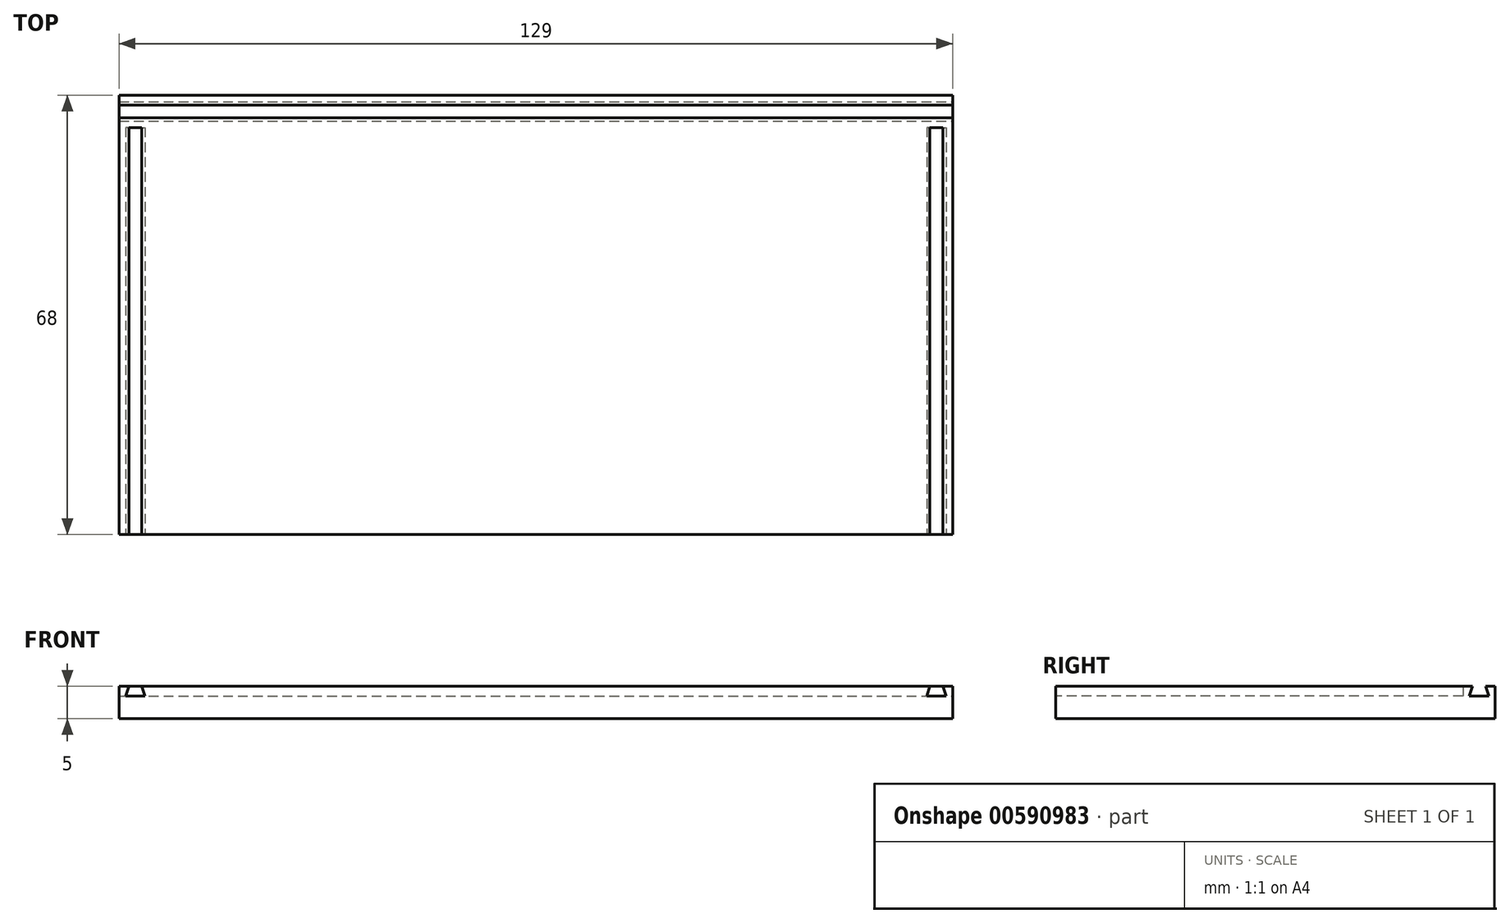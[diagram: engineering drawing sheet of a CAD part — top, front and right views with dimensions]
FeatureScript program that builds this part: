
annotation { "Feature Type Name" : "Feature", "Feature Type Description" : "" }
export const myFeature = defineFeature(function(context is Context, id is Id, definition is map)
    precondition{}
    {
        {
            var Q0;
            Q0=qCreatedBy(makeId("Top.planeOp"),FACE);
            var sketch = newSketch(context, id + "F0", { "sketchPlane" : qUnion([Q0])});
            skLineSegment(sketch, "E0.bottom", {"start": v(64.5, 34) * mm, "end": v(-64.5, 34) * mm});
            skLineSegment(sketch, "E0.top", {"start": v(64.5, -34) * mm, "end": v(-64.5, -34) * mm});
            skLineSegment(sketch, "E0.left", {"start": v(64.5, 34) * mm, "end": v(64.5, -34) * mm});
            skLineSegment(sketch, "E0.right", {"start": v(-64.5, 34) * mm, "end": v(-64.5, -34) * mm});
            skPoint(sketch, "E0.middle", {"position": v(0, 0) * mm});
            skSolve(sketch);
        }
        {
            var Q0;
            Q0=makeQuery(id+"F0.imprint","IMPRINT",FACE,{"disambiguationData":[TD([[makeQuery(id+"F0.imprint","IMPRINT",EDGE,{"derivedFrom":sQuery(id+"F0.wireOp",EDGE,"E0.bottom")}),1.0]])]});
            extrude(context, id + "F1", {"entities" : qUnion([Q0]), "depth" : 5 * mm, "offsetDistance" : 25 * mm});
        }
        {
            var Q0;
            Q0=makeQuery(id+"F1.opExtrude","SWEPT_FACE",FACE,{"disambiguationData":[OSD([sQuery(id+"F0.wireOp",EDGE,"E0.top")])]});
            var sketch = newSketch(context, id + "F2", { "sketchPlane" : qUnion([Q0])});
            skLineSegment(sketch, "E1", {"start": v(-63, 5) * mm, "end": v(-63.5, 3.5) * mm});
            skLineSegment(sketch, "E2", {"start": v(-63.5, 3.5) * mm, "end": v(-60.5, 3.5) * mm});
            skLineSegment(sketch, "E3", {"start": v(-60.5, 3.5) * mm, "end": v(-61, 5) * mm});
            skLineSegment(sketch, "E4", {"start": v(-61, 5) * mm, "end": v(-63, 5) * mm});
            skLineSegment(sketch, "E5", {"start": v(61, 5) * mm, "end": v(60.5, 3.5) * mm});
            skLineSegment(sketch, "E6", {"start": v(60.5, 3.5) * mm, "end": v(63.5, 3.5) * mm});
            skLineSegment(sketch, "E7", {"start": v(63.5, 3.5) * mm, "end": v(63, 5) * mm});
            skLineSegment(sketch, "E8", {"start": v(63, 5) * mm, "end": v(61, 5) * mm});
            skSolve(sketch);
        }
        {
            var Q0;
            Q0=makeQuery(id+"F2.imprint","IMPRINT",FACE,{"disambiguationData":[TD([[makeQuery(id+"F2.imprint","IMPRINT",EDGE,{"derivedFrom":sQuery(id+"F2.wireOp",EDGE,"E5")}),1.0]])]});
            var Q1;
            Q1=makeQuery(id+"F2.imprint","IMPRINT",FACE,{"disambiguationData":[TD([[makeQuery(id+"F2.imprint","IMPRINT",EDGE,{"derivedFrom":sQuery(id+"F2.wireOp",EDGE,"E1")}),1.0]])]});
            extrude(context, id + "F3", {"entities" : qUnion([Q0, Q1]), "operationType" : NewBodyOperationType.REMOVE, "oppositeDirection" : true, "depth" : 63 * mm, "offsetDistance" : 25 * mm});
        }
        {
            var Q0;
            Q0=makeQuery(id+"F1.opExtrude","SWEPT_FACE",FACE,{"disambiguationData":[OSD([sQuery(id+"F0.wireOp",EDGE,"E0.left")])]});
            var sketch = newSketch(context, id + "F4", { "sketchPlane" : qUnion([Q0])});
            skLineSegment(sketch, "E9", {"start": v(32.5, 5) * mm, "end": v(33, 3.5) * mm});
            skLineSegment(sketch, "E10", {"start": v(33, 3.5) * mm, "end": v(30, 3.5) * mm});
            skLineSegment(sketch, "E11", {"start": v(30, 3.5) * mm, "end": v(30.5, 5) * mm});
            skLineSegment(sketch, "E12", {"start": v(30.5, 5) * mm, "end": v(32.5, 5) * mm});
            skLineSegment(sketch, "E13.0", {"start": v(34, 5) * mm, "end": v(34, 0) * mm});
            skSolve(sketch);
        }
        {
            var Q0;
            Q0 = qSketchRegion(id + "F4", true);
            extrude(context, id + "F5", {"entities" : qUnion([Q0]), "operationType" : NewBodyOperationType.REMOVE, "endBound" : BoundingType.THROUGH_ALL, "oppositeDirection" : true, "depth" : 25 * mm, "offsetDistance" : 25 * mm});
        }
    });
